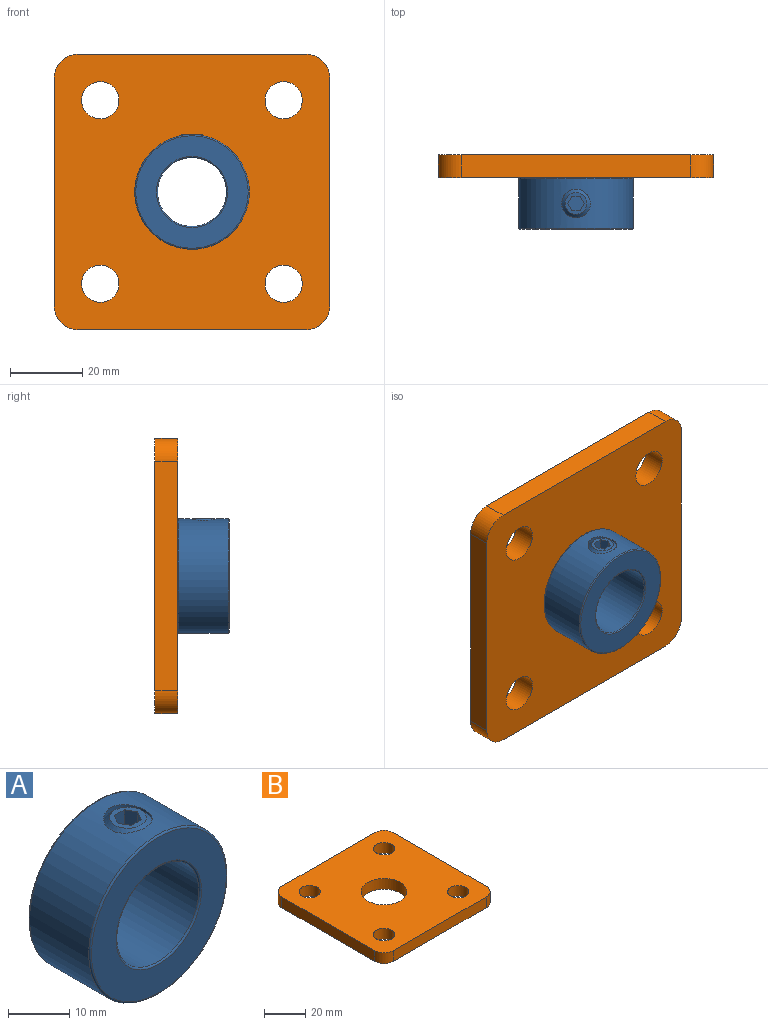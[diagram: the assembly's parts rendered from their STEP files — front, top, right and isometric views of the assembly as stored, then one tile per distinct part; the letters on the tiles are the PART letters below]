
ASSEMBLY  parts=2 mates=1
PART A: 22 faces, bbox 34.4x14.3x34.4 mm
  f0: plane 6.02x6.02mm, normal (0,0,1), area 14.8mm2, adj f1,f2,f3,f4,f5,f6,f7
  f1: cone r=3.01mm half-angle=45deg, axis (0,0,-1), area 29.7mm2, adj f0,f14
  f2: plane 3.97x1.98mm, normal (-0.87,-0.5,0), area 9.1mm2, adj f0,f3,f7,f8
  f3: plane 3.97x1.98mm, normal (-0.87,0.5,0), area 9.1mm2, adj f0,f2,f4,f8
  f4: plane 3.97x2.29mm, normal (0,1,0), area 9.1mm2, adj f0,f3,f5,f8
  f5: plane 3.97x1.98mm, normal (0.87,0.5,0), area 9.1mm2, adj f0,f4,f6,f8
  f6: plane 3.97x1.98mm, normal (0.87,-0.5,0), area 9.1mm2, adj f0,f5,f7,f8
  f7: plane 3.97x2.29mm, normal (0,-1,0), area 9.1mm2, adj f0,f2,f6,f8
  f8: plane 4.58x3.97mm, normal (0,0,1), area 13.6mm2, adj f2,f3,f4,f5,f6,f7
  f9: cylinder r=3.97mm len=7.94mm, axis (0,0,-1), area 34.6mm2, adj f13,f21
  f10: plane 31.12x31.12mm, normal (0,-1,0), area 456mm2, adj f16,f18
  f11: plane 31.12x31.12mm, normal (0,1,0), area 456mm2, adj f15,f17
  f12: cylinder r=15.88mm len=31.75mm, axis (0,1,0), area 1311.8mm2, adj f14,f17,f18
  f13: cylinder r=9.53mm len=19.05mm, axis (0,1,0), area 766.5mm2, adj f9,f15,f16
  f14: cylinder r=3.97mm len=7.94mm, axis (0,0,-1), area 17.6mm2, adj f1,f12
  f15: torus R=9.84mm, axis (0,-1,0), area 30.2mm2, adj f11,f13
  f16: torus R=9.84mm, axis (0,-1,0), area 30.2mm2, adj f10,f13
  f17: torus R=15.56mm, axis (0,-1,0), area 49.4mm2, adj f11,f12
  f18: torus R=15.56mm, axis (0,-1,0), area 49.4mm2, adj f10,f12
  f19: cone r=1.15mm half-angle=45deg, axis (0,0,-1), area 5.9mm2, adj f20
  f20: plane 6.02x6.02mm, normal (0,0,-1), area 24.3mm2, adj f19,f21
  f21: cone r=3.97mm half-angle=45deg, axis (0,0,1), area 29.7mm2, adj f9,f20
PART B: 15 faces, bbox 76.2x76.2x6.4 mm
  f0: plane 63.5x6.35mm, normal (0,-1,0), area 403.2mm2, adj f4,f5,f10,f13
  f1: plane 63.5x6.35mm, normal (1,0,0), area 403.2mm2, adj f4,f5,f10,f11
  f2: plane 63.5x6.35mm, normal (0,1,0), area 403.2mm2, adj f4,f5,f11,f12
  f3: plane 63.5x6.35mm, normal (-1,0,0), area 403.2mm2, adj f4,f5,f12,f13
  f4: plane 76.2x76.2mm, normal (0,0,-1), area 5054.2mm2, adj f0,f1,f2,f3,f6,f7,f8,f9
  f5: plane 76.2x76.2mm, normal (0,0,1), area 5054.2mm2, adj f0,f1,f2,f3,f6,f7,f8,f9
  f6: cylinder r=5.16mm len=10.31mm, axis (0,0,1), area 205.7mm2, adj f4,f5
  f7: cylinder r=5.16mm len=10.31mm, axis (0,0,1), area 205.7mm2, adj f4,f5
  f8: cylinder r=5.16mm len=10.31mm, axis (0,0,1), area 205.7mm2, adj f4,f5
  f9: cylinder r=5.16mm len=10.31mm, axis (0,0,1), area 205.7mm2, adj f4,f5
  f10: cylinder r=6.35mm len=6.35mm, axis (0,0,1), area 63.3mm2, adj f0,f1,f4,f5
  f11: cylinder r=6.35mm len=6.35mm, axis (0,0,-1), area 63.3mm2, adj f1,f2,f4,f5
  f12: cylinder r=6.35mm len=6.35mm, axis (0,0,1), area 63.3mm2, adj f2,f3,f4,f5
  f13: cylinder r=6.35mm len=6.35mm, axis (0,0,-1), area 63.3mm2, adj f0,f3,f4,f5
  f14: cylinder r=11.05mm len=22.1mm, axis (0,0,-1), area 440.8mm2, adj f4,f5
PLACE A at identity fixed
PLACE B rot(axis=(1,0,0),90deg) t=(0,7.14,0)mm
MATE fastened B.f14 <-> A.f12  axis (0,-1,0) through (0,7.14,0)mm
